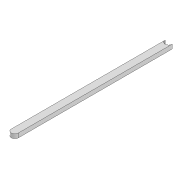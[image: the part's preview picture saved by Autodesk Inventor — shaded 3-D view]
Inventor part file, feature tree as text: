
AUTODESK INVENTOR PART (.ipt)
format: ipt  version: 2022 (Build 260153000, 153)  size: 81,408 bytes
history: native  units: mm
features: extrude x1, sketch x1
ambient origin geometry x8: Origin, YZ Plane, XZ Plane, XY Plane, X Axis, Y Axis, Z Axis, Center Point
bodies: Solid1 (feature_tree)
feature tree (2):
  extrude  "Extrusion1"  Depth=10.0mm
  sketch  "Sketch1"  dims[d0=220.0mm d1=10.0mm d2=6.0mm d3=0.0mm]
